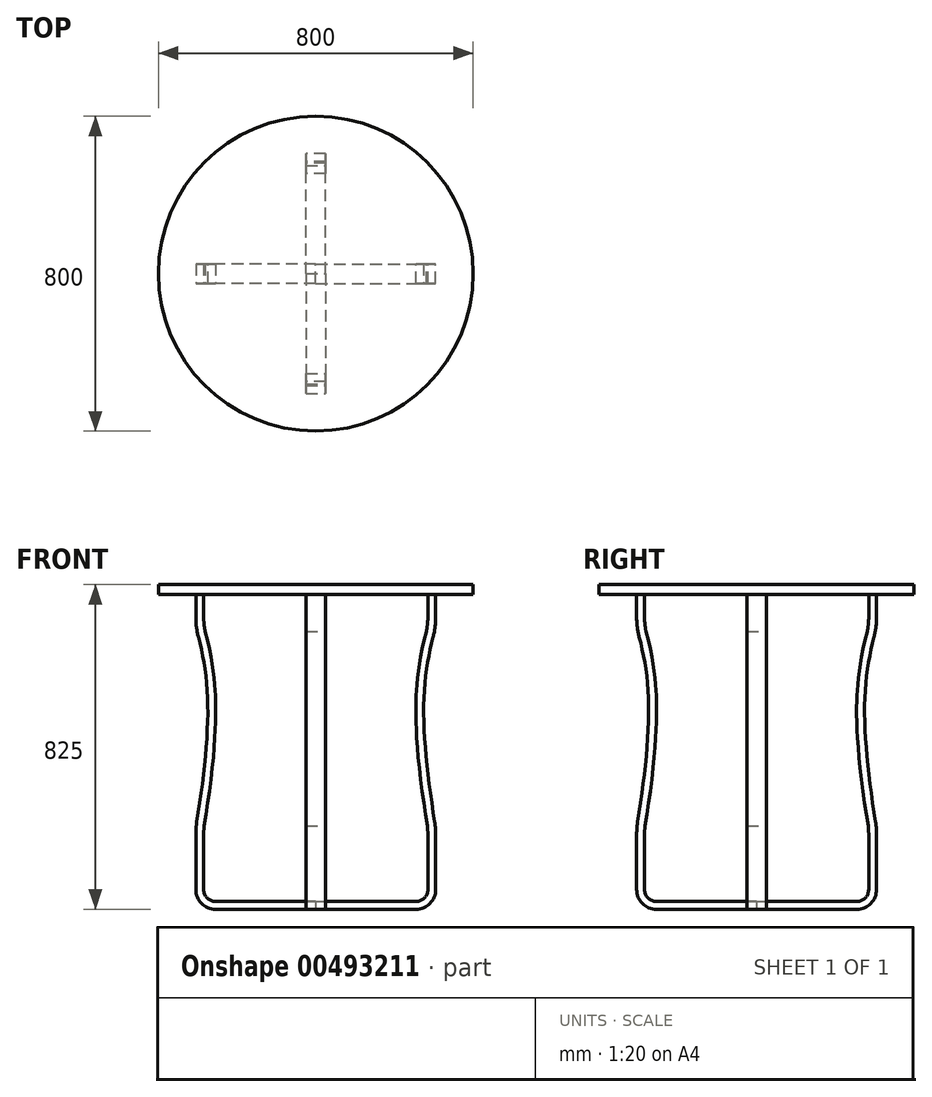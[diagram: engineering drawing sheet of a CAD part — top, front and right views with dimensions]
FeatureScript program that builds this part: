
annotation { "Feature Type Name" : "Feature", "Feature Type Description" : "" }
export const myFeature = defineFeature(function(context is Context, id is Id, definition is map)
    precondition{}
    {
        {
            var Q0;
            Q0=qCreatedBy(makeId("Top.planeOp"),FACE);
            cPlane(context, id + "F0", {"entities" : qUnion([Q0]), "cplaneType" : CPlaneType.OFFSET, "offset" : 800 * mm, "width" : 150 * mm, "height" : 150 * mm});
        }
        {
            var Q0;
            Q0=qCreatedBy(id+"F0.planeOp",FACE);
            var sketch = newSketch(context, id + "F1", { "sketchPlane" : qUnion([Q0])});
            skCircle(sketch, "E0", {"center": v(0, 0) * mm, "radius": 400 * mm});
            skSolve(sketch);
        }
        {
            var Q0;
            Q0 = qSketchRegion(id + "F1", true);
            extrude(context, id + "F2", {"entities" : qUnion([Q0]), "depth" : 25 * mm});
        }
        {
            var Q0;
            Q0=qCreatedBy(makeId("Front.planeOp"),FACE);
            var sketch = newSketch(context, id + "F3", { "sketchPlane" : qUnion([Q0])});
            skLineSegment(sketch, "E1", {"start": v(0, 0) * mm, "end": v(254.75, 0) * mm});
            skFitSpline(sketch, "E2", {"points": [v(331.54, 799.28) * mm, v(275.13, 544.45) * mm, v(341.27, 0) * mm], "startDerivative": vector(-189.2, -563.86) * mm, "endDerivative": vector(185.72, -1007.56) * mm});
            skLineSegment(sketch, "E3", {"start": v(304.75, 50) * mm, "end": v(304.75, 190.04) * mm});
            skPoint(sketch, "E4.orphan", {"position": v(609.5, 0) * mm});
            skLineSegment(sketch, "E5", {"start": v(304.75, 799.28) * mm, "end": v(304.75, 742.38) * mm});
            skPoint(sketch, "E6.visualSharp", {"position": v(304.75, 715.41) * mm});
            skArc(sketch, "E6.filletArc", {"start": v(298.24, 691.8) * mm, "mid": v(303.11, 716.88) * mm, "end": v(304.75, 742.38) * mm});
            skPoint(sketch, "E7.visualSharp", {"position": v(304.75, 206.02) * mm});
            skArc(sketch, "E7.filletArc", {"start": v(304.75, 190.04) * mm, "mid": v(304.12, 205.8) * mm, "end": v(302.26, 221.46) * mm});
            skPoint(sketch, "E8.visualSharp", {"position": v(304.75, 0) * mm});
            skArc(sketch, "E8.filletArc", {"start": v(254.75, 0) * mm, "mid": v(290.1, 14.64) * mm, "end": v(304.75, 50) * mm});
            skLineSegment(sketch, "E9.0", {"start": v(0, 20) * mm, "end": v(254.75, 20) * mm});
            skArc(sketch, "E9.1", {"start": v(254.75, 20) * mm, "mid": v(275.96, 28.79) * mm, "end": v(284.75, 50) * mm});
            skLineSegment(sketch, "E9.2", {"start": v(284.75, 50) * mm, "end": v(284.75, 190.04) * mm});
            skLineSegment(sketch, "E9.3", {"start": v(284.75, 799.28) * mm, "end": v(284.75, 742.38) * mm});
            skArc(sketch, "E9.4", {"start": v(278.9, 696.86) * mm, "mid": v(283.28, 719.43) * mm, "end": v(284.75, 742.38) * mm});
            skFitSpline(sketch, "E9.5", {"points": [v(312.58, 805.65) * mm, v(308.64, 793.9) * mm, v(300.72, 770.3) * mm, v(289.2, 734.08) * mm, v(278.5, 696.52) * mm, v(270.7, 663.7) * mm, v(265.36, 636.27) * mm, v(261.87, 615.07) * mm, v(258.96, 593.18) * mm, v(257.06, 574.3) * mm, v(255.9, 558.8) * mm, v(255.2, 546.97) * mm, v(254.68, 534.92) * mm, v(254.25, 518.6) * mm, v(254.15, 497.74) * mm, v(254.7, 471.99) * mm, v(255.9, 445.56) * mm, v(258.25, 409.47) * mm, v(262.56, 362.87) * mm, v(269.59, 304.9) * mm, v(278.16, 245.2) * mm, v(287.95, 184.15) * mm, v(302.24, 101.4) * mm, v(313.86, 38.36) * mm, v(321.6, -3.63) * mm]});
            skArc(sketch, "E9.6", {"start": v(284.75, 190.04) * mm, "mid": v(284.19, 204.22) * mm, "end": v(282.51, 218.32) * mm});
            skLineSegment(sketch, "E10", {"start": v(304.75, 799.28) * mm, "end": v(284.75, 799.28) * mm});
            skLineSegment(sketch, "E11", {"start": v(0, 20) * mm, "end": v(0, 0) * mm});
            skSolve(sketch);
        }
        {
            var Q0;
            Q0 = qSketchRegion(id + "F3", true);
            extrude(context, id + "F4", {"entities" : qUnion([Q0]), "endBound" : BoundingType.SYMMETRIC, "depth" : 50 * mm});
        }
        {
            var Q0;
            Q0=makeQuery(id+"F4.opExtrude","SWEPT_BODY",BODY,{"disambiguationData":[OSD([sQuery(id+"F3.wireOp",EDGE,"E1"),sQuery(id+"F3.wireOp",EDGE,"E2"),sQuery(id+"F3.wireOp",EDGE,"E3"),sQuery(id+"F3.wireOp",EDGE,"E5"),sQuery(id+"F3.wireOp",EDGE,"E6.filletArc"),sQuery(id+"F3.wireOp",EDGE,"E7.filletArc"),sQuery(id+"F3.wireOp",EDGE,"E8.filletArc"),sQuery(id+"F3.wireOp",EDGE,"E9.0"),sQuery(id+"F3.wireOp",EDGE,"E9.1"),sQuery(id+"F3.wireOp",EDGE,"E9.2"),sQuery(id+"F3.wireOp",EDGE,"E9.3"),sQuery(id+"F3.wireOp",EDGE,"E9.4"),sQuery(id+"F3.wireOp",EDGE,"E9.5"),sQuery(id+"F3.wireOp",EDGE,"E9.6"),sQuery(id+"F3.wireOp",EDGE,"E10"),sQuery(id+"F3.wireOp",EDGE,"E11")])]});
            var Q1;
            Q1=makeQuery(id+"F2.opExtrude","SWEPT_FACE",FACE,{"disambiguationData":[OSD([sQuery(id+"F1.wireOp",EDGE,"E0")])]});
            circularPattern(context, id + "F5", {"entities" : qUnion([Q0]), "axis" : qUnion([Q1]), "angle" : 360 * degree, "instanceCount" : 4, "equalSpace" : true});
        }
    });
